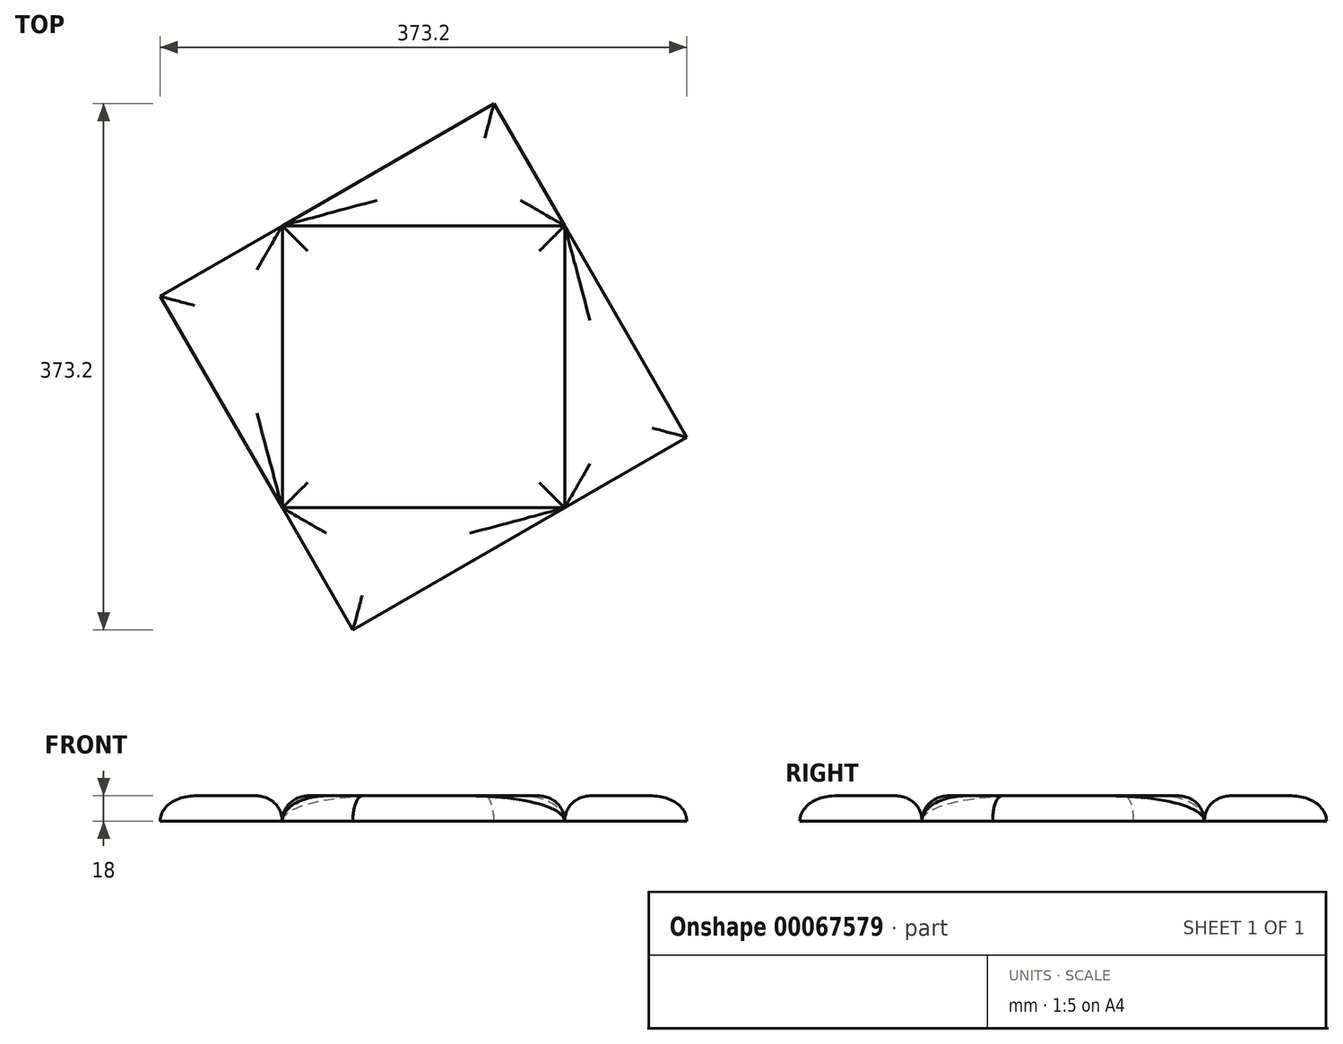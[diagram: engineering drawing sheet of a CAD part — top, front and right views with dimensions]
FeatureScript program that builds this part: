
annotation { "Feature Type Name" : "Feature", "Feature Type Description" : "" }
export const myFeature = defineFeature(function(context is Context, id is Id, definition is map)
    precondition{}
    {
        {
            var Q0;
            Q0=qCreatedBy(makeId("Top.planeOp"),FACE);
            var sketch = newSketch(context, id + "F0", { "sketchPlane" : qUnion([Q0])});
            skLineSegment(sketch, "E0.rect.bottom", {"start": v(100, -100) * mm, "end": v(-100, -100) * mm});
            skLineSegment(sketch, "E0.rect.top", {"start": v(100, 100) * mm, "end": v(-100, 100) * mm});
            skLineSegment(sketch, "E0.rect.left", {"start": v(100, -100) * mm, "end": v(100, 100) * mm});
            skLineSegment(sketch, "E0.rect.right", {"start": v(-100, -100) * mm, "end": v(-100, 100) * mm});
            skPoint(sketch, "E0.rect.middle", {"position": v(0, 0) * mm});
            skLineSegment(sketch, "E1", {"start": v(100, 100) * mm, "end": v(186.6, -50) * mm});
            skLineSegment(sketch, "E2", {"start": v(186.6, -50) * mm, "end": v(100, -100) * mm});
            skLineSegment(sketch, "E3.1.0", {"start": v(50, 186.6) * mm, "end": v(100, 100) * mm});
            skLineSegment(sketch, "E3.1.1", {"start": v(-100, 100) * mm, "end": v(50, 186.6) * mm});
            skLineSegment(sketch, "E3.2.0", {"start": v(-186.6, 50) * mm, "end": v(-100, 100) * mm});
            skLineSegment(sketch, "E3.2.1", {"start": v(-100, -100) * mm, "end": v(-186.6, 50) * mm});
            skLineSegment(sketch, "E3.3.0", {"start": v(-50, -186.6) * mm, "end": v(-100, -100) * mm});
            skLineSegment(sketch, "E3.3.1", {"start": v(100, -100) * mm, "end": v(-50, -186.6) * mm});
            skSolve(sketch);
        }
        {
            var Q0;
            Q0=makeQuery(id+"F0.imprint","IMPRINT",FACE,{"disambiguationData":[TD([[makeQuery(id+"F0.imprint","IMPRINT",EDGE,{"derivedFrom":sQuery(id+"F0.wireOp",EDGE,"E0.rect.bottom")}),-1.0]])]});
            extrude(context, id + "F1", {"entities" : qUnion([Q0]), "depth" : 18 * mm});
        }
        {
            var Q0;
            Q0=makeQuery(id+"F0.imprint","IMPRINT",FACE,{"disambiguationData":[TD([[makeQuery(id+"F0.imprint","IMPRINT",EDGE,{"derivedFrom":sQuery(id+"F0.wireOp",EDGE,"E0.rect.right")}),1.0]])]});
            var Q1;
            Q1=makeQuery(id+"F0.imprint","IMPRINT",FACE,{"disambiguationData":[TD([[makeQuery(id+"F0.imprint","IMPRINT",EDGE,{"derivedFrom":sQuery(id+"F0.wireOp",EDGE,"E0.rect.top")}),-1.0]])]});
            var Q2;
            Q2=makeQuery(id+"F0.imprint","IMPRINT",FACE,{"disambiguationData":[TD([[makeQuery(id+"F0.imprint","IMPRINT",EDGE,{"derivedFrom":sQuery(id+"F0.wireOp",EDGE,"E0.rect.left")}),-1.0]])]});
            var Q3;
            Q3=makeQuery(id+"F0.imprint","IMPRINT",FACE,{"disambiguationData":[TD([[makeQuery(id+"F0.imprint","IMPRINT",EDGE,{"derivedFrom":sQuery(id+"F0.wireOp",EDGE,"E0.rect.bottom")}),1.0]])]});
            extrude(context, id + "F2", {"entities" : qUnion([Q0, Q1, Q2, Q3]), "depth" : 18 * mm});
        }
        {
            var Q0;
            Q0=makeQuery(id+"F1.opExtrude","CAP_FACE",FACE,{"disambiguationData":[OSD([sQuery(id+"F0.wireOp",EDGE,"E0.rect.bottom"),sQuery(id+"F0.wireOp",EDGE,"E0.rect.top"),sQuery(id+"F0.wireOp",EDGE,"E0.rect.left"),sQuery(id+"F0.wireOp",EDGE,"E0.rect.right")])],"isStart":false});
            var Q1;
            Q1=makeQuery(id+"F2.opExtrude","CAP_FACE",FACE,{"disambiguationData":[OSD([sQuery(id+"F0.wireOp",EDGE,"E0.rect.top"),sQuery(id+"F0.wireOp",EDGE,"E3.1.0"),sQuery(id+"F0.wireOp",EDGE,"E3.1.1")])],"isStart":false});
            var Q2;
            Q2=makeQuery(id+"F2.opExtrude","CAP_FACE",FACE,{"disambiguationData":[OSD([sQuery(id+"F0.wireOp",EDGE,"E0.rect.left"),sQuery(id+"F0.wireOp",EDGE,"E1"),sQuery(id+"F0.wireOp",EDGE,"E2")])],"isStart":false});
            var Q3;
            Q3=makeQuery(id+"F2.opExtrude","CAP_FACE",FACE,{"disambiguationData":[OSD([sQuery(id+"F0.wireOp",EDGE,"E0.rect.bottom"),sQuery(id+"F0.wireOp",EDGE,"E3.3.0"),sQuery(id+"F0.wireOp",EDGE,"E3.3.1")])],"isStart":false});
            var Q4;
            Q4=makeQuery(id+"F2.opExtrude","CAP_FACE",FACE,{"disambiguationData":[OSD([sQuery(id+"F0.wireOp",EDGE,"E0.rect.right"),sQuery(id+"F0.wireOp",EDGE,"E3.2.0"),sQuery(id+"F0.wireOp",EDGE,"E3.2.1")])],"isStart":false});
            fillet(context, id + "F3", {"entities" : qUnion([Q0, Q1, Q2, Q3, Q4]), "radius" : 18 * mm, "tangentPropagation" : true, "allowEdgeOverflow" : false});
        }
    });
